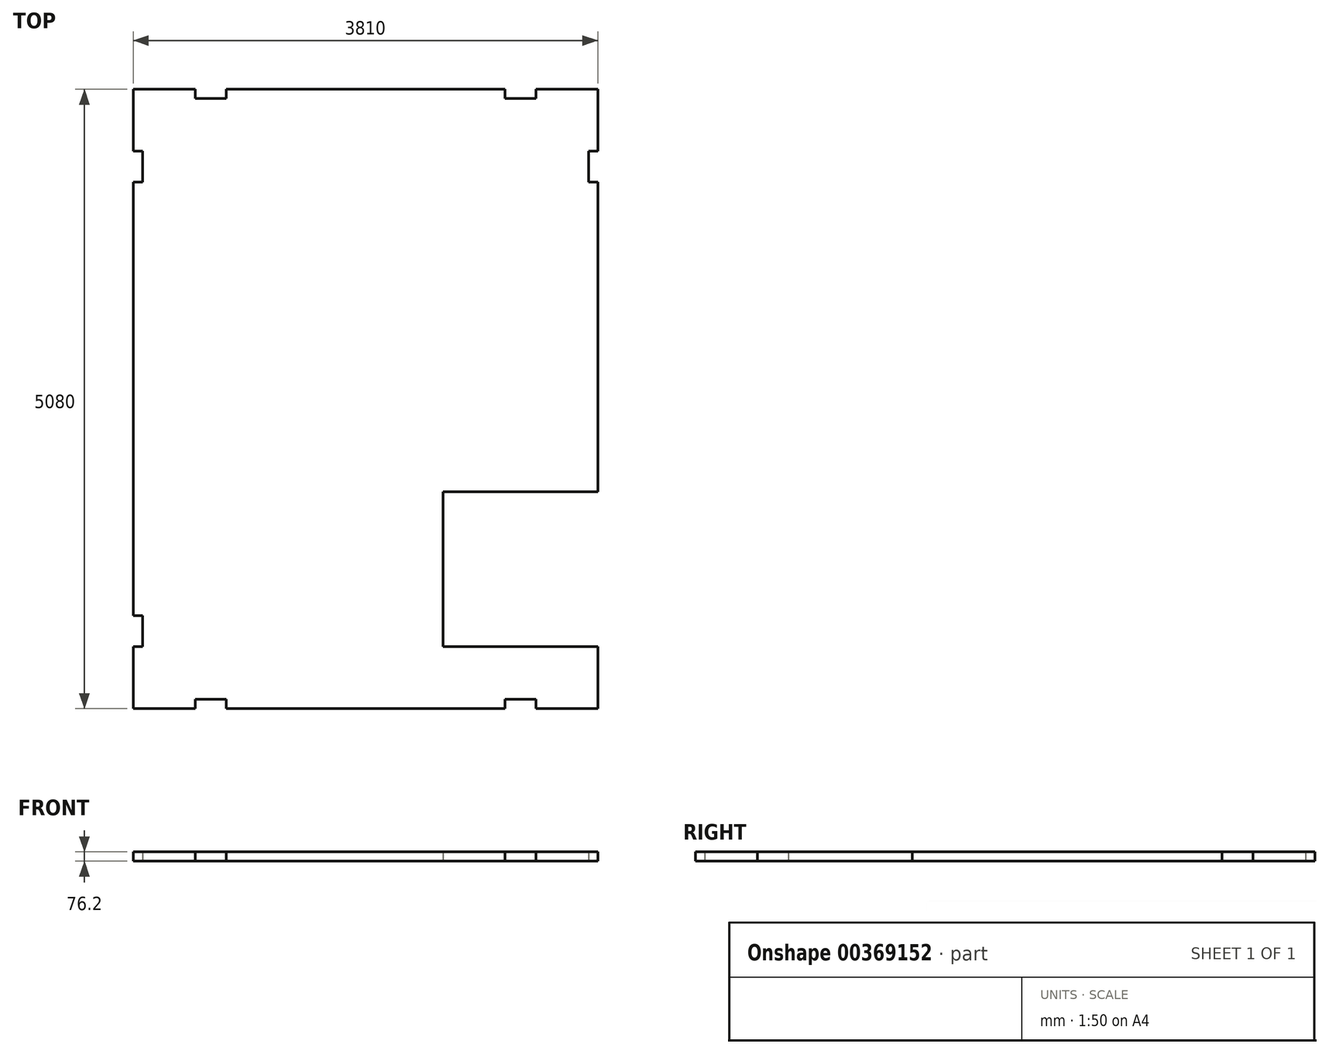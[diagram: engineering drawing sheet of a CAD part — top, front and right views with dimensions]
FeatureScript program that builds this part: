
annotation { "Feature Type Name" : "Feature", "Feature Type Description" : "" }
export const myFeature = defineFeature(function(context is Context, id is Id, definition is map)
    precondition{}
    {
        {
            var Q0;
            Q0=qCreatedBy(makeId("Top.planeOp"),FACE);
            var sketch = newSketch(context, id + "F0", { "sketchPlane" : qUnion([Q0])});
            skLineSegment(sketch, "E0.bottom", {"start": v(1905, 2540) * mm, "end": v(1397, 2540) * mm});
            skLineSegment(sketch, "E0.top", {"start": v(1143, -2540) * mm, "end": v(-1143, -2540) * mm});
            skLineSegment(sketch, "E0.left", {"start": v(1905, 2540) * mm, "end": v(1905, 2032) * mm});
            skLineSegment(sketch, "E0.right", {"start": v(-1905, 2540) * mm, "end": v(-1905, 2032) * mm});
            skPoint(sketch, "E0.middle", {"position": v(0, 0) * mm});
            skLineSegment(sketch, "E1", {"start": v(-1905, 1778) * mm, "end": v(-1828.8, 1778) * mm});
            skLineSegment(sketch, "E2", {"start": v(-1905, 2032) * mm, "end": v(-1828.8, 2032) * mm});
            skLineSegment(sketch, "E3", {"start": v(-1828.8, 2032) * mm, "end": v(-1828.8, 1778) * mm});
            skLineSegment(sketch, "E4.trimOffspring", {"start": v(-1905, 1778) * mm, "end": v(-1905, -1778) * mm});
            skLineSegment(sketch, "E5", {"start": v(-1905, 2540) * mm, "end": v(-1397, 2540) * mm});
            skLineSegment(sketch, "E6", {"start": v(-1397, 2540) * mm, "end": v(-1143, 2540) * mm});
            skLineSegment(sketch, "E7", {"start": v(-1397, 2540) * mm, "end": v(-1397, 2463.8) * mm});
            skLineSegment(sketch, "E8", {"start": v(-1397, 2463.8) * mm, "end": v(-1143, 2463.8) * mm});
            skLineSegment(sketch, "E9", {"start": v(-1143, 2540) * mm, "end": v(-1143, 2463.8) * mm});
            skLineSegment(sketch, "E10", {"start": v(-1905, -2540) * mm, "end": v(-1905, -2032) * mm});
            skLineSegment(sketch, "E11", {"start": v(-1905, -2032) * mm, "end": v(-1828.8, -2032) * mm});
            skLineSegment(sketch, "E12", {"start": v(-1905, -1778) * mm, "end": v(-1828.8, -1778) * mm});
            skLineSegment(sketch, "E13", {"start": v(-1828.8, -1778) * mm, "end": v(-1828.8, -2032) * mm});
            skLineSegment(sketch, "E14", {"start": v(-1905, -2540) * mm, "end": v(-1397, -2540) * mm});
            skLineSegment(sketch, "E15", {"start": v(-1397, -2540) * mm, "end": v(-1397, -2463.8) * mm});
            skLineSegment(sketch, "E16", {"start": v(-1397, -2463.8) * mm, "end": v(-1143, -2463.8) * mm});
            skLineSegment(sketch, "E17", {"start": v(-1143, -2463.8) * mm, "end": v(-1143, -2540) * mm});
            skLineSegment(sketch, "E18.trimOffspring", {"start": v(-1397, -2540) * mm, "end": v(-1905, -2540) * mm});
            skLineSegment(sketch, "E19", {"start": v(1905, -2540) * mm, "end": v(1397, -2540) * mm});
            skLineSegment(sketch, "E20", {"start": v(1397, -2540) * mm, "end": v(1397, -2463.8) * mm});
            skLineSegment(sketch, "E21", {"start": v(1397, -2463.8) * mm, "end": v(1143, -2463.8) * mm});
            skLineSegment(sketch, "E22", {"start": v(1143, -2463.8) * mm, "end": v(1143, -2540) * mm});
            skLineSegment(sketch, "E23", {"start": v(1905, -2540) * mm, "end": v(1905, -2032) * mm});
            skLineSegment(sketch, "E24", {"start": v(1905, -2032) * mm, "end": v(635, -2032) * mm});
            skLineSegment(sketch, "E25", {"start": v(635, -2032) * mm, "end": v(635, -762) * mm});
            skLineSegment(sketch, "E26", {"start": v(635, -762) * mm, "end": v(1905, -762) * mm});
            skLineSegment(sketch, "E27.trimOffspring", {"start": v(1905, -2032) * mm, "end": v(1905, -2540) * mm});
            skLineSegment(sketch, "E28", {"start": v(1905, 2032) * mm, "end": v(1828.8, 2032) * mm});
            skLineSegment(sketch, "E29", {"start": v(1828.8, 2032) * mm, "end": v(1828.8, 1778) * mm});
            skLineSegment(sketch, "E30", {"start": v(1905, 1778) * mm, "end": v(1828.8, 1778) * mm});
            skLineSegment(sketch, "E31.trimOffspring", {"start": v(1905, 1778) * mm, "end": v(1905, -762) * mm});
            skLineSegment(sketch, "E32", {"start": v(1397, 2540) * mm, "end": v(1397, 2463.8) * mm});
            skLineSegment(sketch, "E33", {"start": v(1143, 2540) * mm, "end": v(1143, 2463.8) * mm});
            skLineSegment(sketch, "E34", {"start": v(1397, 2463.8) * mm, "end": v(1143, 2463.8) * mm});
            skLineSegment(sketch, "E35.trimOffspring", {"start": v(1143, 2540) * mm, "end": v(-1905, 2540) * mm});
            skLineSegment(sketch, "E36.trimOffspring", {"start": v(-1905, -2032) * mm, "end": v(-1905, -2540) * mm});
            skSolve(sketch);
        }
        {
            var Q0;
            Q0=makeQuery(id+"F0.imprint","IMPRINT",FACE,{"disambiguationData":[TD([[makeQuery(id+"F0.imprint","IMPRINT",EDGE,{"derivedFrom":sQuery(id+"F0.wireOp",EDGE,"E0.top")}),-1.0]])]});
            extrude(context, id + "F1", {"entities" : qUnion([Q0]), "depth" : 76.2 * mm});
        }
    });
